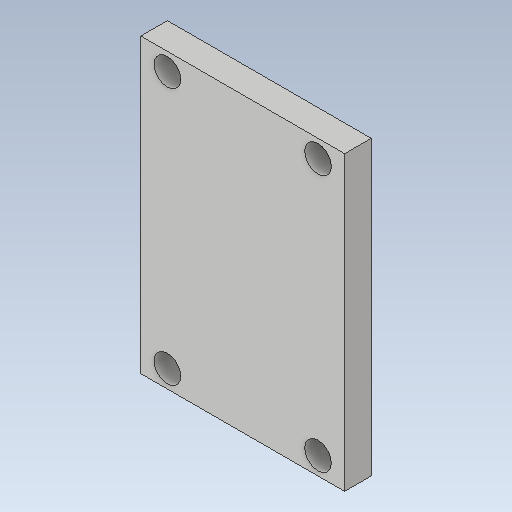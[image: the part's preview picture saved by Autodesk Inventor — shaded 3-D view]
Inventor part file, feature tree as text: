
AUTODESK INVENTOR PART (.ipt)
format: ipt  version: 2020.1 (Build 241239000, 239)  size: 115,200 bytes
history: native  units: mm
features: extrude x2, sketch x2
ambient origin geometry x8: Origin, YZ Plane, XZ Plane, XY Plane, X Axis, Y Axis, Z Axis, Center Point
bodies: Solid1 (feature_tree)
feature tree (4):
  extrude  "Extrusion1"  Depth=33.0mm
  extrude  "Extrusion2"  Depth=3.0mm
  sketch  "Sketch1"  dims[d0=23.0mm d1=33.0mm]
  sketch  "Sketch2"  dims[d2=3.0mm d3=0.0mm d4=3.0mm d5=2.0mm d6=3.0mm d7=3.0mm d8=2.0mm d9=3.0mm d10=2.0mm d11=3.0mm d12=2.0mm d13=3.0mm d14=3.0mm d15=3.0mm d16=3.0mm d17=0.0mm]
